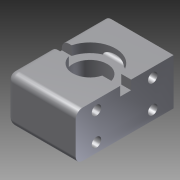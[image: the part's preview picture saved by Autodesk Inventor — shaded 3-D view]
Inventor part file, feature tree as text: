
AUTODESK INVENTOR PART (.ipt)
format: ipt  version: 2012 (Build 160160000, 160)  size: 183,808 bytes
history: native  units: mm
features: extrude x6, sketch x6, fillet x4
ambient origin geometry x8: Origin, YZ Plane, XZ Plane, XY Plane, X Axis, Y Axis, Z Axis, Center Point
bodies: Solid1 (feature_tree)
feature tree (16):
  extrude  "Extrusion1"  Depth=30.0mm
  extrude  "Extrusion6"  Depth=21.2mm
  fillet  "Fillet3"  Radius=15.0mm
  fillet  "Fillet4"  Radius=20.0mm
  extrude  "Extrusion7"  Depth=4.0mm
  extrude  "Extrusion3"  Depth=4.0mm
  extrude  "Extrusion4"  Depth=9.0mm
  extrude  "Extrusion5"  Depth=9.0mm
  fillet  "Fillet1"  Radius=9.0mm
  fillet  "Fillet2"  Radius=4.1mm
  sketch  "Sketch1"  dims[d0=42.4mm d1=30.0mm]
  sketch  "Sketch2"  dims[d2=15.0mm d3=21.2mm d4=15.0mm d5=20.0mm d6=0.0mm]
  sketch  "Sketch3"  dims[d7=4.1mm d8=4.0mm]
  sketch  "Sketch4"  dims[d9=4.0mm d10=4.0mm]
  sketch  "Sketch5"  dims[d11=4.0mm d12=9.0mm]
  sketch  "Sketch6"  dims[d13=9.0mm d14=9.0mm d15=9.0mm d18=4.1mm d19=5.0mm d20=5.0mm d21=10.0mm d22=10.0mm d23=20.0mm d24=0.0mm d25=7.5mm d26=4.0mm d27=0.0mm d28=7.5mm d30=6.0mm d31=0.0mm d32=3.0mm d33=1.0mm d34=10.0mm d35=0.0mm d36=3.0mm d37=3.0mm d38=4.0mm d39=0.0mm]
